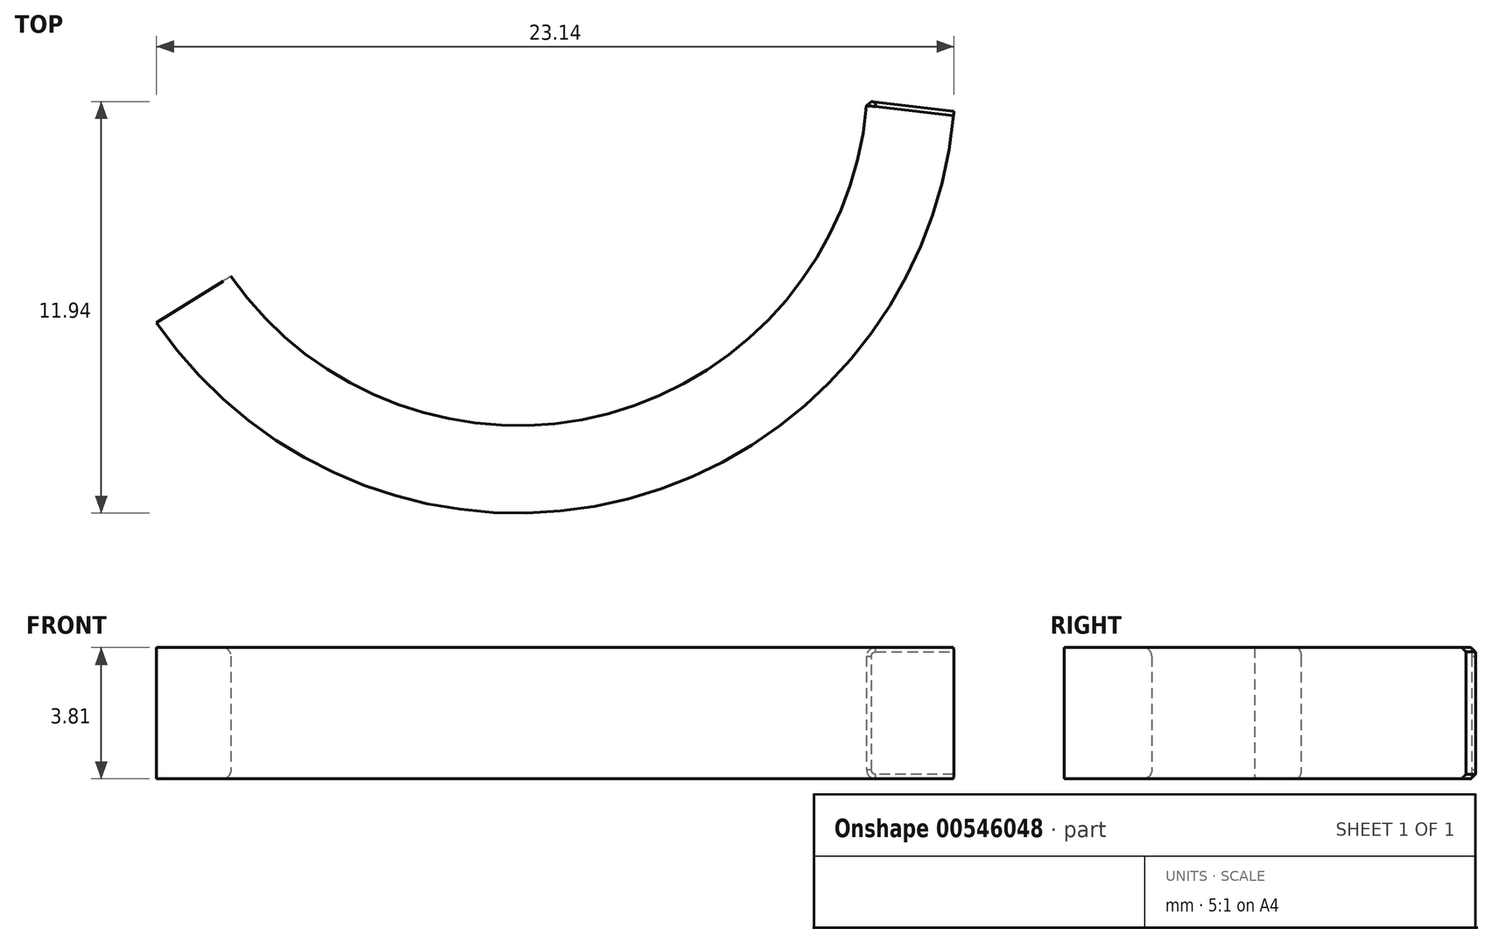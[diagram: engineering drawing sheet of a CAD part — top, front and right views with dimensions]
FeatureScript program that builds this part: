
annotation { "Feature Type Name" : "Feature", "Feature Type Description" : "" }
export const myFeature = defineFeature(function(context is Context, id is Id, definition is map)
    precondition{}
    {
        {
            var Q0;
            Q0=qCreatedBy(makeId("Top.planeOp"),FACE);
            var sketch = newSketch(context, id + "F0", { "sketchPlane" : qUnion([Q0])});
            skArc(sketch, "E0", {"start": v(20.32, -0.14) * mm, "mid": v(13.15, -9.71) * mm, "end": v(1.84, -5.83) * mm});
            skArc(sketch, "E1", {"start": v(18.44, -9.63) * mm, "mid": v(20.5, -7.37) * mm, "end": v(21.97, -4.68) * mm});
            skLineSegment(sketch, "E2", {"start": v(1.84, -5.83) * mm, "end": v(-0.9, -7.54) * mm});
            skArc(sketch, "E3", {"start": v(18.44, -9.63) * mm, "mid": v(8.5, -12.6) * mm, "end": v(-0.32, -7.17) * mm});
            skLineSegment(sketch, "E4", {"start": v(20.32, -0.14) * mm, "end": v(22.86, 0) * mm});
            skLineSegment(sketch, "E5", {"start": v(20.24, -1.31) * mm, "end": v(22.74, -1.72) * mm});
            skLineSegment(sketch, "E6", {"start": v(20.07, -2.23) * mm, "end": v(22.57, -2.69) * mm});
            skLineSegment(sketch, "E7", {"start": v(21.97, -4.68) * mm, "end": v(19.67, -3.58) * mm});
            skLineSegment(sketch, "E8", {"start": v(13.78, -9.5) * mm, "end": v(15.3, -11.62) * mm});
            skArc(sketch, "E9", {"start": v(21.97, -4.68) * mm, "mid": v(22.31, -3.7) * mm, "end": v(22.57, -2.69) * mm});
            skArc(sketch, "E10", {"start": v(22.57, -2.69) * mm, "mid": v(22.67, -2.2) * mm, "end": v(22.74, -1.72) * mm});
            skLineSegment(sketch, "E11", {"start": v(20.3, -0.75) * mm, "end": v(22.8, -1.04) * mm});
            skArc(sketch, "E12", {"start": v(22.57, -2.69) * mm, "mid": v(22.74, -1.77) * mm, "end": v(22.83, -0.84) * mm});
            skLineSegment(sketch, "E13", {"start": v(22.8, -1.04) * mm, "end": v(22.83, -1.05) * mm});
            skSolve(sketch);
        }
        {
            var Q0;
            Q0 = qSketchRegion(id + "F0", true);
            extrude(context, id + "F1", {"entities" : qUnion([Q0]), "depth" : 3.8 * mm, "offsetDistance" : 25.4 * mm});
        }
        {
            var Q0;
            Q0=makeQuery(id+"F1.opExtrude","CAP_EDGE",EDGE,{"disambiguationData":[OSD([sQuery(id+"F0.wireOp",EDGE,"E0")])],"isStart":false});
            var Q1;
            Q1=makeQuery(id+"F1.opExtrude","CAP_EDGE",EDGE,{"disambiguationData":[OSD([sQuery(id+"F0.wireOp",EDGE,"E0")])],"isStart":true});
            fillet(context, id + "F2", {"entities" : qUnion([Q0, Q1]), "radius" : 0.25 * mm, "tangentPropagation" : true, "allowEdgeOverflow" : false});
        }
        {
            var Q0;
            Q0=makeQuery(id+"F1.opExtrude","SWEPT_EDGE",EDGE,{"disambiguationData":[OSD([sQuery(id+"F0.wireOp",EDGE,"E0"),sQuery(id+"F0.wireOp",EDGE,"E11")])]});
            chamfer(context, id + "F3", {"entities" : qUnion([Q0]), "width" : 0.13 * mm, "tangentPropagation" : true});
        }
    });
